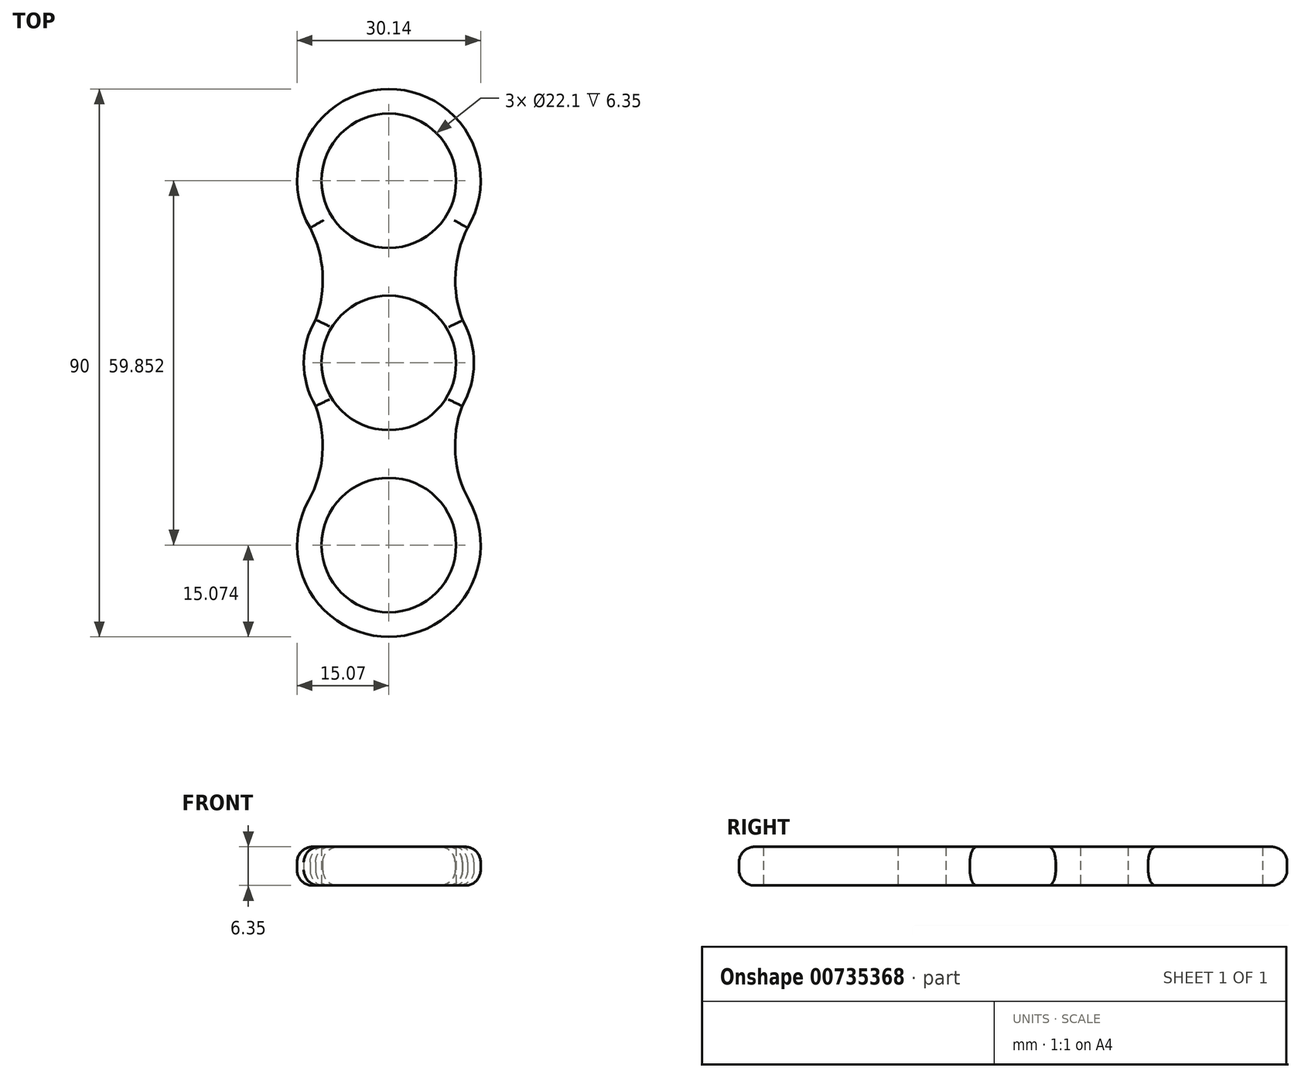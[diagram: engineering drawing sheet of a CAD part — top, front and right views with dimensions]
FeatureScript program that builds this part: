
annotation { "Feature Type Name" : "Feature", "Feature Type Description" : "" }
export const myFeature = defineFeature(function(context is Context, id is Id, definition is map)
    precondition{}
    {
        {
            var Q0;
            Q0=qCreatedBy(makeId("Top.planeOp"),FACE);
            var sketch = newSketch(context, id + "F0", { "sketchPlane" : qUnion([Q0])});
            skCircle(sketch, "E0", {"center": v(0, 0) * mm, "radius": 11.05 * mm});
            skCircle(sketch, "E1", {"center": v(0, 0) * mm, "radius": 13.97 * mm});
            skCircle(sketch, "E2", {"center": v(0, 29.93) * mm, "radius": 11.05 * mm});
            skCircle(sketch, "E3", {"center": v(0, 29.93) * mm, "radius": 15.07 * mm});
            skCircle(sketch, "E4.1.0", {"center": v(0, -29.93) * mm, "radius": 11.05 * mm});
            skCircle(sketch, "E4.1.1", {"center": v(0, -29.93) * mm, "radius": 15.07 * mm});
            skArc(sketch, "E5", {"start": v(12.94, 22.2) * mm, "mid": v(10.9, 13.33) * mm, "end": v(13.21, 4.53) * mm});
            skArc(sketch, "E6", {"start": v(-13.21, 4.53) * mm, "mid": v(-10.86, 13.33) * mm, "end": v(-12.94, 22.2) * mm});
            skArc(sketch, "E7", {"start": v(-13.21, -22.67) * mm, "mid": v(-10.87, -13.6) * mm, "end": v(-13.21, -4.53) * mm});
            skArc(sketch, "E8", {"start": v(13.21, -4.53) * mm, "mid": v(10.87, -13.6) * mm, "end": v(13.21, -22.67) * mm});
            skSolve(sketch);
        }
        {
            var Q0;
            Q0 = qSketchRegion(id + "F0", true);
            extrude(context, id + "F1", {"entities" : qUnion([Q0]), "depth" : 6.35 * mm, "offsetDistance" : 25.4 * mm});
        }
        {
            var Q0;
            Q0=makeQuery(id+"F1.opExtrude","CAP_EDGE",EDGE,{"disambiguationData":[OSD([sQuery(id+"F0.wireOp",EDGE,"E3")])],"isStart":false});
            var Q1;
            Q1=makeQuery(id+"F1.opExtrude","CAP_EDGE",EDGE,{"disambiguationData":[OSD([sQuery(id+"F0.wireOp",EDGE,"E6")])],"isStart":false});
            var Q2;
            {var subQ0=sQuery(id+"F0.wireOp",EDGE,"E7");var subQ1=sQuery(id+"F0.wireOp",EDGE,"E1");var subQ2=makeQuery(id+"F0.imprint","INTERSECT",VERTEX,{"disambiguationData":[OD(0.0)],"derivedFrom":[subQ1,subQ0]});var subQ3=sQuery(id+"F0.wireOp",EDGE,"E6");var subQ4=makeQuery(id+"F0.imprint","INTERSECT",VERTEX,{"disambiguationData":[OD(0.0)],"derivedFrom":[subQ1,subQ3]});Q2=makeQuery(id+"F1.opExtrude","CAP_EDGE",EDGE,{"disambiguationData":[OSD([subQ1]),TDD([makeQuery(id+"F0.imprint","IMPRINT",EDGE,{"disambiguationData":[TD([[subQ4,1.0]])],"derivedFrom":subQ1}),makeQuery(id+"F0.imprint","IMPRINT",EDGE,{"disambiguationData":[TD([[subQ4,-1.0]])],"derivedFrom":subQ1}),makeQuery(id+"F0.imprint","IMPRINT",EDGE,{"disambiguationData":[TD([[subQ2,-1.0]])],"derivedFrom":subQ1})])],"isStart":false});}
            var Q3;
            {var subQ0=sQuery(id+"F0.wireOp",EDGE,"E5");var subQ1=sQuery(id+"F0.wireOp",EDGE,"E1");var subQ2=makeQuery(id+"F0.imprint","INTERSECT",VERTEX,{"disambiguationData":[OD(0.0)],"derivedFrom":[subQ1,subQ0]});var subQ3=sQuery(id+"F0.wireOp",EDGE,"E8");var subQ4=makeQuery(id+"F0.imprint","INTERSECT",VERTEX,{"disambiguationData":[OD(0.0)],"derivedFrom":[subQ1,subQ3]});Q3=makeQuery(id+"F1.opExtrude","CAP_EDGE",EDGE,{"disambiguationData":[OSD([subQ1]),TDD([makeQuery(id+"F0.imprint","IMPRINT",EDGE,{"disambiguationData":[TD([[subQ2,-1.0]])],"derivedFrom":subQ1}),makeQuery(id+"F0.imprint","IMPRINT",EDGE,{"disambiguationData":[TD([[subQ4,1.0]])],"derivedFrom":subQ1}),makeQuery(id+"F0.imprint","IMPRINT",EDGE,{"disambiguationData":[TD([[subQ2,1.0]])],"derivedFrom":subQ1})])],"isStart":false});}
            var Q4;
            Q4=makeQuery(id+"F1.opExtrude","CAP_EDGE",EDGE,{"disambiguationData":[OSD([sQuery(id+"F0.wireOp",EDGE,"E8")])],"isStart":false});
            var Q5;
            Q5=makeQuery(id+"F1.opExtrude","CAP_EDGE",EDGE,{"disambiguationData":[OSD([sQuery(id+"F0.wireOp",EDGE,"E5")])],"isStart":false});
            var Q6;
            Q6=makeQuery(id+"F1.opExtrude","CAP_EDGE",EDGE,{"disambiguationData":[OSD([sQuery(id+"F0.wireOp",EDGE,"E7")])],"isStart":false});
            var Q7;
            Q7=makeQuery(id+"F1.opExtrude","CAP_EDGE",EDGE,{"disambiguationData":[OSD([sQuery(id+"F0.wireOp",EDGE,"E4.1.1")])],"isStart":false});
            var Q8;
            Q8=makeQuery(id+"F1.opExtrude","CAP_EDGE",EDGE,{"disambiguationData":[OSD([sQuery(id+"F0.wireOp",EDGE,"E3")])],"isStart":true});
            var Q9;
            Q9=makeQuery(id+"F1.opExtrude","CAP_EDGE",EDGE,{"disambiguationData":[OSD([sQuery(id+"F0.wireOp",EDGE,"E6")])],"isStart":true});
            var Q10;
            {var subQ0=sQuery(id+"F0.wireOp",EDGE,"E7");var subQ1=sQuery(id+"F0.wireOp",EDGE,"E1");var subQ2=makeQuery(id+"F0.imprint","INTERSECT",VERTEX,{"disambiguationData":[OD(0.0)],"derivedFrom":[subQ1,subQ0]});var subQ3=sQuery(id+"F0.wireOp",EDGE,"E6");var subQ4=makeQuery(id+"F0.imprint","INTERSECT",VERTEX,{"disambiguationData":[OD(0.0)],"derivedFrom":[subQ1,subQ3]});Q10=makeQuery(id+"F1.opExtrude","CAP_EDGE",EDGE,{"disambiguationData":[OSD([subQ1]),TDD([makeQuery(id+"F0.imprint","IMPRINT",EDGE,{"disambiguationData":[TD([[subQ4,1.0]])],"derivedFrom":subQ1}),makeQuery(id+"F0.imprint","IMPRINT",EDGE,{"disambiguationData":[TD([[subQ4,-1.0]])],"derivedFrom":subQ1}),makeQuery(id+"F0.imprint","IMPRINT",EDGE,{"disambiguationData":[TD([[subQ2,-1.0]])],"derivedFrom":subQ1})])],"isStart":true});}
            var Q11;
            Q11=makeQuery(id+"F1.opExtrude","CAP_EDGE",EDGE,{"disambiguationData":[OSD([sQuery(id+"F0.wireOp",EDGE,"E7")])],"isStart":true});
            var Q12;
            Q12=makeQuery(id+"F1.opExtrude","CAP_EDGE",EDGE,{"disambiguationData":[OSD([sQuery(id+"F0.wireOp",EDGE,"E4.1.1")])],"isStart":true});
            var Q13;
            Q13=makeQuery(id+"F1.opExtrude","CAP_EDGE",EDGE,{"disambiguationData":[OSD([sQuery(id+"F0.wireOp",EDGE,"E8")])],"isStart":true});
            var Q14;
            {var subQ0=sQuery(id+"F0.wireOp",EDGE,"E5");var subQ1=sQuery(id+"F0.wireOp",EDGE,"E1");var subQ2=makeQuery(id+"F0.imprint","INTERSECT",VERTEX,{"disambiguationData":[OD(0.0)],"derivedFrom":[subQ1,subQ0]});var subQ3=sQuery(id+"F0.wireOp",EDGE,"E8");var subQ4=makeQuery(id+"F0.imprint","INTERSECT",VERTEX,{"disambiguationData":[OD(0.0)],"derivedFrom":[subQ1,subQ3]});Q14=makeQuery(id+"F1.opExtrude","CAP_EDGE",EDGE,{"disambiguationData":[OSD([subQ1]),TDD([makeQuery(id+"F0.imprint","IMPRINT",EDGE,{"disambiguationData":[TD([[subQ2,-1.0]])],"derivedFrom":subQ1}),makeQuery(id+"F0.imprint","IMPRINT",EDGE,{"disambiguationData":[TD([[subQ4,1.0]])],"derivedFrom":subQ1}),makeQuery(id+"F0.imprint","IMPRINT",EDGE,{"disambiguationData":[TD([[subQ2,1.0]])],"derivedFrom":subQ1})])],"isStart":true});}
            var Q15;
            Q15=makeQuery(id+"F1.opExtrude","CAP_EDGE",EDGE,{"disambiguationData":[OSD([sQuery(id+"F0.wireOp",EDGE,"E5")])],"isStart":true});
            fillet(context, id + "F2", {"entities" : qUnion([Q0, Q1, Q2, Q3, Q4, Q5, Q6, Q7, Q8, Q9, Q10, Q11, Q12, Q13, Q14, Q15]), "radius" : 2.54 * mm, "tangentPropagation" : true, "allowEdgeOverflow" : false});
        }
    });
